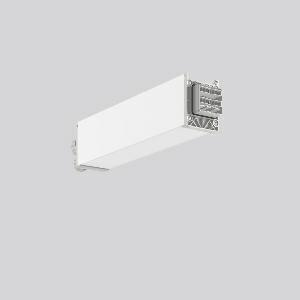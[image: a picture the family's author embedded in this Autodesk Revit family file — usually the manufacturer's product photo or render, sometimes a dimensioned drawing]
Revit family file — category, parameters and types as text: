
# Revit family: linedo_anfangseinspeisung_14pol_s_982678_002_1_19f8
name_source: partatom
category: Lighting Fixtures
units: mm (PartAtom-declared; Revit-internal decimal feet)

## family parameters
Cut with Voids When Loaded = No
Host = Face
Light Source = No
Part Type = Normal
Room Calculation Point = No
Round Connector Dimension = Use Diameter
Shared = No

## types (1)
- LINEDO_Anfangseinspeisung_14pol_S
    Apparent Load = 0 VA
    Default Elevation = 1800 mm
    Description = Series: LINEDO
Initial power feed, 14-pole, connection plug. Housing: extruded aluminium profile, powder-coated. Cover made of plastic, surface like housing. LINEDO plug system, plastic, light grey. 2 cable glands (M20 and M25). Cable glands on side or on top. Easy connection for rigid or flexible wires.
Colour: white
Length: 330 mm
Width: 58 mm
Height: 76 mm
Weight: 728 g
    Height = 76 mm
    Lamp = 0 x
    Length = 312 mm
    Luminous efficacy = 0 lm/W
    Manufacturer = RZB
    ModVariant = No
    Model = 982678.002.1
    Mounting Place = Ceiling
    Mounting Type = Surface mounted, Pendant
    Number of Poles = 1
    OnlyDefault = Yes
    Power Factor = 1
    Product Name = LINEDO_Anfangseinspeisung_14pol_S
    Product group = Continuous line luminaire system Linedo IP 54
    ProductGroupID = 314
    Protection Class = Protection class I
    Protection Degree = IP 54
    RLX_Detail_Level = 1
    RLX_Emergency_Light_Flux = 0 lm
    RLX_Emergency_Type = 0
    RLX_Emergency_Type_DB = No
    RlxData = <blob elided: 12173 chars, md5=d3069662>
    Standby Power = 0 W
    System Light Flux = 0 lm
    System Power = 0 W
    Type Comments = Product without accessories
    Type Image = 982678.002.1.jpg
    URL = http://relux.com
    VarID = ---
    Voltage = 0 V
    Weight = 0.00 kg
    Width = 58 mm

## geometry (parser evidence)
native form markers: Sweep x9
no freeform markers — native parametric forms only
